# Revit family: 3250 Steel Replica_Fixed
name_source: partatom
category: Windows
units: mm (PartAtom-declared; Revit-internal decimal feet)

## family parameters
Always vertical = Yes
Cut with Voids When Loaded = No
Host = Wall
OmniClass Number = 23.30.20.00
OmniClass Title = Windows
Room Calculation Point = No
Shared = No

## types (1)
- 3250 Steel Replica_Fixed
    Default Sill Height = 3' - 0"
    Depth From Exterior = 0' - 2"
    Equal Bay Height = 1' - 7 9/32"
    Equal Bay Width = 0' - 11 9/32"
    Frame Material = <By Category>
    Glass Material = Glass
    Height = 5' - 0"
    Horizontal Member Array = 2
    Horizontal Member Array Vis = Yes
    Horizontal Member Length = 2' - 10 3/8"
    Keep Horiztonal Member Mid = 2' - 5 1/16"
    Rough Width = 3' - 0"
    Single Horizontal Member Vis = Yes
    Single Vertical Member Vis = Yes
    Vertical Member Array = 2
    Vertical Member Array Vis = Yes
    Vertical Member Length = 4' - 10 3/8"
    Wall Closure = By host
    Width = 3' - 0"

## geometry (parser evidence)
native form markers: Sweep x6
no freeform markers — native parametric forms only
